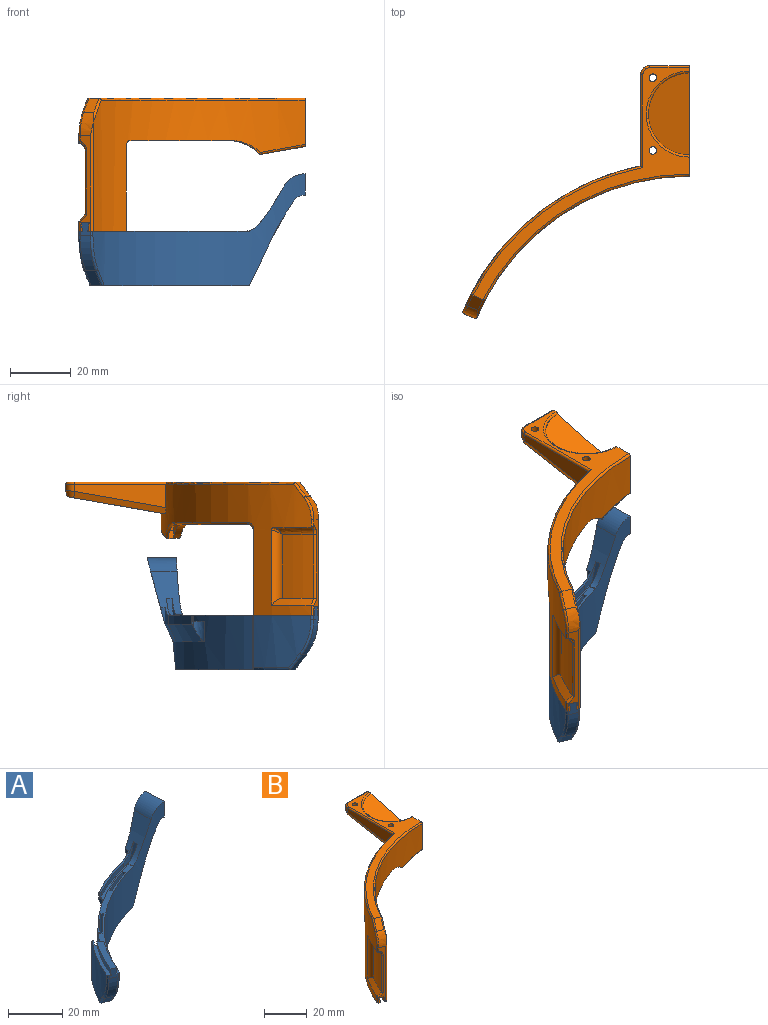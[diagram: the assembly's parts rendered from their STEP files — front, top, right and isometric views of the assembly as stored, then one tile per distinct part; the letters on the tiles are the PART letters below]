
ASSEMBLY  parts=2 mates=1
PART A: 55 faces, bbox 77.2x59.5x43.8 mm
  f0: cylinder r=76mm len=70.02mm, axis (0,0,1), area 1419.7mm2, adj f1,f2,f3,f4,f5,f6,f7,f8
  f1: bspline ~15.94x5.21mm, area 13.4mm2, adj f0,f2,f12,f13
  f2: bspline ~5.88x4.26mm, area 7.1mm2, adj f0,f1,f3,f14
  f3: plane 52.48x39.61mm, normal (0,0,-1), area 144.6mm2, adj f0,f2,f4,f14,f15,f16,f17,f18
  f4: extruded ~24.09x12.06mm, area 101.9mm2, adj f0,f3,f5,f21,f30,f31
  f5: extruded ~7.42x3.86mm, area 31.6mm2, adj f0,f4,f6,f30
  f6: cylinder r=4.5mm len=7.8mm, axis (0,-1,0), area 33.5mm2, adj f0,f5,f7,f30
  f7: plane 9.58x7mm, normal (1,0,0), area 60.5mm2, adj f0,f6,f8,f30
  f8: cylinder r=8mm len=9.92mm, axis (0,-1,0), area 81.2mm2, adj f0,f7,f9,f30
  f9: extruded ~14.5x12.67mm, area 116.9mm2, adj f0,f8,f10,f21,f30,f32,f33,f34
  f10: plane 2.24x0.56mm, normal (-0.97,-0.24,0), area 0.4mm2, adj f0,f9,f11,f21
  f11: plane 56.26x46.84mm, normal (0,0,1), area 162mm2, adj f0,f10,f12,f17,f18,f19,f20,f21
  f12: cylinder r=0.7mm len=1.45mm, axis (0,0,1), area 1.6mm2, adj f0,f1,f11,f38
  f13: cylinder r=18mm len=11.57mm, axis (0.92,-0.38,0), area 45.3mm2, adj f1,f14,f38,f44
  f14: plane 5.27x5.1mm, normal (-0.29,-0.71,-0.64), area 23.5mm2, adj f2,f3,f13,f15
  f15: bspline ~21.32x16.58mm, area 7.3mm2, adj f3,f14,f16,f39,f44
  f16: torus R=80.3mm, axis (0,0,1), area 15.8mm2, adj f3,f15,f17,f39
  f17: cylinder r=0.7mm len=18mm, axis (0,0,1), area 19.6mm2, adj f3,f11,f16,f18,f39
  f18: plane 18x0.08mm, normal (0.63,0.78,0), area 1.7mm2, adj f3,f11,f17,f19
  f19: cylinder r=80.2mm len=18mm, axis (0,0,1), area 62.8mm2, adj f3,f11,f18,f20
  f20: plane 18x1.53mm, normal (0.59,0.8,0), area 34.2mm2, adj f3,f11,f19,f21
  f21: cylinder r=78.3mm len=50.25mm, axis (0,0,1), area 850.1mm2, adj f3,f4,f9,f10,f11,f20,f31,f32
  f22: plane 18x0.89mm, normal (0.89,0.46,0), area 18mm2, adj f3,f11,f23,f25
  f23: cylinder r=76.7mm len=18mm, axis (0,0,1), area 229.5mm2, adj f3,f11,f22,f24
  f24: plane 18x0.95mm, normal (-0.95,-0.3,0), area 18mm2, adj f3,f11,f23,f25
  f25: cylinder r=77.7mm len=18mm, axis (0,0,1), area 232.5mm2, adj f3,f11,f22,f24
  f26: plane 18x0.74mm, normal (0.67,0.74,0), area 18mm2, adj f3,f11,f27,f29
  f27: cylinder r=76.7mm len=18mm, axis (0,0,1), area 222.6mm2, adj f3,f11,f26,f28
  f28: plane 18x0.78mm, normal (-0.78,-0.62,0), area 18mm2, adj f3,f11,f27,f29
  f29: cylinder r=77.7mm len=18mm, axis (0,0,1), area 225.5mm2, adj f3,f11,f26,f28
  f30: plane 22.15x15.89mm, normal (0,0.97,-0.26), area 133mm2, adj f4,f5,f6,f7,f8,f9,f31,f33
  f31: plane 6.55x4.24mm, normal (0,0.91,-0.42), area 18.4mm2, adj f4,f21,f30,f33
  f32: plane 7.45x2.41mm, normal (-0.95,0,0.31), area 15.1mm2, adj f9,f21,f37,f49
  f33: plane 11.41x4.35mm, normal (-1,0,0), area 5.1mm2, adj f9,f21,f30,f31,f34,f48
  f34: plane 5.63x0.06mm, normal (0.98,0.19,0), area 0.3mm2, adj f9,f33,f35,f48
  f35: cylinder r=81mm len=5.49mm, axis (0,0,1), area 20.5mm2, adj f9,f34,f48,f50
  f36: revolved ~19.91x8.54mm, area 16.8mm2, adj f9,f50,f51,f52,f53
  f37: cylinder r=80.2mm len=7.5mm, axis (0,0,1), area 18.5mm2, adj f9,f32,f45,f49,f51
  f38: plane 4.27x3.33mm, normal (-0.38,-0.92,0), area 11.6mm2, adj f11,f12,f13,f40,f41,f43,f54
  f39: cylinder r=81mm len=18.89mm, axis (0,0,1), area 337.8mm2, adj f11,f15,f16,f17,f40,f44
  f40: cylinder r=0.7mm len=1.45mm, axis (0,0,1), area 1.6mm2, adj f11,f38,f39,f44
  f41: cone r=79.4mm half-angle=6.9deg, axis (0,0,1), area 51.4mm2, adj f11,f38,f42,f54
  f42: plane 2.82x2.12mm, normal (0.58,0.82,0), area 6.4mm2, adj f11,f41,f43,f54
  f43: cone r=77.2mm half-angle=6.9deg, axis (0,0,-1), area 49.9mm2, adj f11,f38,f42,f54
  f44: bspline ~14.88x5.84mm, area 13.8mm2, adj f13,f15,f39,f40
  f45: plane 26.18x12.25mm, normal (0,0,1), area 50.3mm2, adj f21,f37,f46,f49,f51,f52,f53
  f46: cylinder r=4mm len=6.79mm, axis (0,0,-1), area 19.2mm2, adj f21,f45,f47,f53
  f47: cone r=78.2mm half-angle=25deg, axis (0,0,1), area 139.3mm2, adj f21,f46,f48,f50,f53
  f48: cone r=81mm half-angle=25deg, axis (0,0,1), area 28.5mm2, adj f21,f33,f34,f35,f47
  f49: plane 1.94x0.06mm, normal (-1,0,0), area 0.1mm2, adj f21,f32,f37,f45
  f50: cylinder r=81mm len=19.34mm, axis (0,0,-1), area 63.9mm2, adj f35,f36,f47,f53
  f51: cylinder r=80.2mm len=19.09mm, axis (0,0,-1), area 42.7mm2, adj f36,f37,f45,f52
  f52: cylinder r=0.5mm len=2.07mm, axis (0,0,-1), area 1.8mm2, adj f36,f45,f51,f53
  f53: cylinder r=0.5mm len=3.73mm, axis (0,0,-1), area 1.8mm2, adj f36,f45,f46,f47,f50,f52
  f54: plane 16.81x10.84mm, normal (0,0,1), area 46.3mm2, adj f38,f41,f42,f43
PART B: 100 faces, bbox 98.9x99.4x59.6 mm
  f0: cylinder r=80mm len=9mm, axis (0,0,-1), area 18mm2, adj f3,f27,f29,f58
  f1: cylinder r=80mm len=45.52mm, axis (0,0,-1), area 452.5mm2, adj f27,f29,f38,f58
  f2: cylinder r=13.5mm len=26.74mm, axis (0,0,1), area 105.8mm2, adj f3,f53,f54,f57,f65,f66,f95
  f3: plane 36.56x16.06mm, normal (1,0,0), area 173mm2, adj f0,f2,f4,f14,f24,f26,f27,f29
  f4: cylinder r=81mm len=74.64mm, axis (0,0,1), area 1376.6mm2, adj f3,f6,f50,f51,f64,f68,f69,f70
  f5: plane 31.63x3.33mm, normal (-0.38,-0.92,0), area 52.4mm2, adj f6,f42,f43,f45,f83,f84,f85,f86
  f6: plane 21.49x15.57mm, normal (0,0,-1), area 70mm2, adj f4,f5,f13,f14,f15,f16,f17,f18
  f7: cylinder r=77.7mm len=11mm, axis (0,0,1), area 50.3mm2, adj f8,f11,f19,f29,f36,f38
  f8: plane 10.07x0.78mm, normal (-0.78,-0.62,0), area 5.7mm2, adj f7,f11,f23,f28,f29,f36
  f9: plane 4x1.78mm, normal (0.89,0.46,0), area 4.5mm2, adj f11,f20,f22,f77,f81
  f10: plane 10.15x0.95mm, normal (-0.95,-0.3,0), area 5.1mm2, adj f20,f22,f30,f37,f46,f78
  f11: plane 35.06x24.88mm, normal (0,0,-1), area 71.7mm2, adj f7,f8,f9,f14,f16,f19,f20,f22
  f12: plane 35.68x24.2mm, normal (0,0,-1), area 4.4mm2, adj f18,f40,f47,f75
  f13: plane 28x0.08mm, normal (0.63,0.78,0), area 2.7mm2, adj f6,f18,f40,f72
  f14: cylinder r=76mm len=70.02mm, axis (0,0,1), area 1850.9mm2, adj f3,f6,f11,f15,f39,f46,f83,f96
  f15: plane 28x1.79mm, normal (0.63,0.78,0), area 64.4mm2, adj f6,f14,f16,f39
  f16: cylinder r=78.3mm len=48.35mm, axis (0,0,1), area 235.5mm2, adj f6,f11,f15,f17,f21,f25,f39,f41
  f17: plane 30x1.53mm, normal (0.59,0.8,0), area 57mm2, adj f6,f16,f18,f41
  f18: cylinder r=80.2mm len=49.52mm, axis (0,0,1), area 241.7mm2, adj f6,f12,f13,f17,f21,f25,f40,f41
  f19: plane 11x0.74mm, normal (0.67,0.74,0), area 10.3mm2, adj f7,f11,f23,f36
  f20: cylinder r=77.7mm len=11.93mm, axis (0,0,1), area 38.8mm2, adj f9,f10,f11,f46,f77
  f21: plane 2.65x1.87mm, normal (-0.98,-0.19,0), area 5mm2, adj f16,f18,f24,f48
  f22: cylinder r=76.7mm len=11.77mm, axis (0,0,1), area 102.3mm2, adj f9,f10,f11,f37,f46,f81
  f23: cylinder r=76.7mm len=9.02mm, axis (0,0,1), area 108.4mm2, adj f8,f11,f19,f36
  f24: plane 15.02x4.98mm, normal (0.17,0,-0.98), area 54mm2, adj f3,f21,f46,f47,f74,f98
  f25: plane 44.76x29.84mm, normal (0,0,-1), area 101mm2, adj f16,f18,f41,f48
  f26: plane 76.53x71.45mm, normal (0,0,1), area 471.2mm2, adj f3,f49,f59,f60,f87,f89,f91,f93
  f27: plane 57.96x28.24mm, normal (0,0,-1), area 180.7mm2, adj f0,f1,f3,f28,f30,f31,f32,f33
  f28: cylinder r=77mm len=12.75mm, axis (0,0,-1), area 86.7mm2, adj f8,f27,f29,f31,f34,f79,f82
  f29: plane 57.96x27.71mm, normal (0,0,1), area 157.7mm2, adj f0,f1,f3,f7,f8,f28,f30,f38
  f30: cylinder r=77mm len=23.35mm, axis (0,0,-1), area 214mm2, adj f3,f10,f27,f29,f32,f78
  f31: plane 0.62x0.32mm, normal (-0.89,-0.46,0), area 0mm2, adj f27,f28,f33,f79
  f32: plane 2.93x0.67mm, normal (0.95,0.3,0), area 1.7mm2, adj f27,f30,f33,f37
  f33: cylinder r=77.7mm len=11.93mm, axis (0,0,-1), area 12.6mm2, adj f27,f31,f32,f37,f79,f81
  f34: plane 2.93x0.55mm, normal (0.78,0.62,0), area 1.7mm2, adj f27,f28,f35,f36
  f35: cylinder r=77.7mm len=9.12mm, axis (0,0,-1), area 25mm2, adj f27,f34,f36,f38
  f36: torus R=79.7mm, axis (0,0,1), area 31.3mm2, adj f7,f8,f19,f23,f34,f35
  f37: torus R=79.7mm, axis (0,0,1), area 19.9mm2, adj f10,f22,f32,f33,f81
  f38: cylinder r=3mm len=9mm, axis (0,0,-1), area 36.6mm2, adj f1,f7,f27,f29,f35
  f39: cylinder r=2mm len=3.07mm, axis (-0.78,0.63,0), area 7.2mm2, adj f11,f14,f15,f16
  f40: cylinder r=2mm len=2mm, axis (-0.78,0.63,0), area 0.3mm2, adj f12,f13,f18,f73
  f41: cylinder r=2mm len=2.75mm, axis (-0.8,0.59,0), area 6mm2, adj f16,f17,f18,f25
  f42: cone r=79.47mm half-angle=6.9deg, axis (0,0,1), area 51.5mm2, adj f5,f6,f44,f45
  f43: cone r=77.13mm half-angle=6.9deg, axis (0,0,-1), area 49.9mm2, adj f5,f6,f44,f45
  f44: plane 2.82x2.23mm, normal (-0.58,-0.82,0), area 6.8mm2, adj f6,f42,f43,f45
  f45: plane 16.89x10.97mm, normal (0,0,-1), area 48.8mm2, adj f5,f42,f43,f44
  f46: bspline ~53.16x20.61mm, area 25.6mm2, adj f10,f11,f14,f16,f20,f22,f24,f98
  f47: bspline ~61x23.06mm, area 1.2mm2, adj f12,f18,f24,f74,f76
  f48: cylinder r=4mm len=4.3mm, axis (0.19,-0.98,0), area 11.9mm2, adj f16,f18,f21,f25
  f49: plane 5.07x4.88mm, normal (-0.29,-0.71,0.64), area 21.9mm2, adj f26,f83,f94,f96,f97
  f50: plane 30.1x7.69mm, normal (-1,0,0), area 151.7mm2, adj f4,f61,f64,f91
  f51: plane 33.03x15.74mm, normal (0,0.17,-0.98), area 473mm2, adj f3,f4,f59,f60,f62,f63,f64
  f52: plane 13x2.01mm, normal (0,1,0), area 26.1mm2, adj f3,f61,f62,f87
  f53: plane 28.39x14.89mm, normal (0,-0.26,0.97), area 300mm2, adj f2,f3,f56,f57,f65,f95
  f54: plane 6.01x3.18mm, normal (-1,0,0), area 16.3mm2, adj f2,f55,f57,f58,f66
  f55: plane 6x4.43mm, normal (0,0,-1), area 10.8mm2, adj f54,f56,f58,f66
  f56: cylinder r=2.5mm len=5mm, axis (0,-1,0), area 25.1mm2, adj f53,f55,f57,f58,f65
  f57: plane 6x4.39mm, normal (0,0,1), area 16.1mm2, adj f2,f53,f54,f56,f58
  f58: bspline ~12.99x12.37mm, area 89mm2, adj f0,f1,f27,f29,f54,f55,f56,f57
  f59: cylinder r=1.25mm len=9.65mm, axis (0,0,1), area 74.9mm2, adj f26,f51
  f60: cylinder r=1.25mm len=5.42mm, axis (0,0,1), area 41.7mm2, adj f26,f51
  f61: cylinder r=3mm len=3mm, axis (0,0,-1), area 10.4mm2, adj f50,f52,f63,f89
  f62: plane 13x2.09mm, normal (0,0.97,-0.23), area 27.9mm2, adj f3,f51,f52,f63
  f63: bspline ~3x3mm, area 8.9mm2, adj f51,f61,f62,f64
  f64: plane 30.47x7.43mm, normal (-0.93,0.07,-0.37), area 70.1mm2, adj f4,f50,f51,f63
  f65: bspline ~6.4x3.87mm, area 7.6mm2, adj f2,f53,f56,f66
  f66: cone r=13.5mm half-angle=45deg, axis (0,0,-1), area 8.7mm2, adj f2,f54,f55,f65
  f67: cylinder r=78.78mm len=21mm, axis (0,0,1), area 243.9mm2, adj f68,f69,f70,f86
  f68: revolved ~13.1x8.31mm, area 46.7mm2, adj f4,f67,f71,f88,f90
  f69: revolved ~13.94x8.84mm, area 43.7mm2, adj f4,f67,f70,f84,f85,f86
  f70: cylinder r=3mm len=24.72mm, axis (0,0,1), area 88.5mm2, adj f4,f67,f69,f71
  f71: bspline ~3.77x2.51mm, area 2.6mm2, adj f4,f68,f70
  f72: cylinder r=0.7mm len=28mm, axis (0,0,1), area 31mm2, adj f4,f6,f13,f73
  f73: bspline ~3.3x2.57mm, area 3.9mm2, adj f4,f40,f72,f75
  f74: bspline ~38.57x7.45mm, area 17mm2, adj f3,f4,f24,f47,f76
  f75: torus R=80.3mm, axis (0,0,1), area 48.2mm2, adj f4,f12,f73,f76
  f76: bspline ~14.29x5.91mm, area 13.4mm2, adj f4,f47,f74,f75
  f77: cone r=77.7mm half-angle=45deg, axis (0,0,1), area 19.1mm2, adj f9,f20,f29,f78
  f78: plane 1.92x1.17mm, normal (-0.67,-0.21,0.71), area 1.7mm2, adj f10,f29,f30,f77
  f79: plane 11.42x7.68mm, normal (0,0,1), area 13.7mm2, adj f28,f31,f33,f80,f81,f82
  f80: plane 8.98x8.48mm, normal (-0.46,0.89,0), area 51.8mm2, adj f29,f79,f81,f82
  f81: plane 9.16x7.51mm, normal (0.68,0.35,-0.64), area 21.4mm2, adj f9,f22,f33,f37,f79,f80
  f82: cylinder r=5mm len=8.98mm, axis (0,0,-1), area 37.4mm2, adj f28,f29,f79,f80
  f83: bspline ~7.71x5.05mm, area 33.7mm2, adj f5,f14,f49,f92,f97,f99
  f84: cylinder r=0.7mm len=3.41mm, axis (0,0,1), area 3.7mm2, adj f4,f5,f6,f69,f85
  f85: bspline ~12.75x11.8mm, area 3.5mm2, adj f5,f69,f84,f86
  f86: cylinder r=0.7mm len=21.29mm, axis (0,0,1), area 23.3mm2, adj f5,f67,f69,f85,f88
  f87: cylinder r=0.7mm len=13mm, axis (-1,0,0), area 14.3mm2, adj f3,f26,f52,f89
  f88: bspline ~3.81x2.85mm, area 4.1mm2, adj f5,f68,f86,f90
  f89: torus R=2.3mm, axis (0,0,1), area 4.7mm2, adj f26,f61,f87,f91
  f90: cylinder r=0.7mm len=2.52mm, axis (0,0,1), area 2.5mm2, adj f4,f5,f68,f88,f92
  f91: cylinder r=0.7mm len=30.67mm, axis (0,-1,0), area 33.4mm2, adj f26,f50,f89,f93
  f92: bspline ~10.08x3.65mm, area 9.1mm2, adj f4,f83,f90,f94
  f93: torus R=80.3mm, axis (0,0,1), area 79.9mm2, adj f4,f26,f91,f94
  f94: bspline ~21.32x16.58mm, area 6.8mm2, adj f4,f26,f49,f92,f93
  f95: torus R=14.2mm, axis (0,0,1), area 47.4mm2, adj f2,f3,f26,f53
  f96: torus R=76.7mm, axis (0,0,1), area 91.5mm2, adj f3,f14,f26,f49,f97
  f97: bspline ~8.24x6.14mm, area 8.5mm2, adj f14,f49,f83,f96
  f98: bspline ~14.94x3.32mm, area 16.1mm2, adj f3,f14,f24,f46
  f99: cylinder r=0.7mm len=35.72mm, axis (0,0,1), area 36.8mm2, adj f5,f6,f14,f83
PLACE A t=(46.12,-60.28,18.6)mm
PLACE B t=(46.17,-60.35,18.6)mm
MATE slider B.f5 <-> A.f38  axis (-0.38,-0.92,0) through (-27.7,-50.97,-10.58)mm
